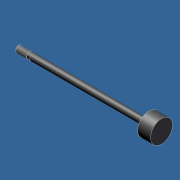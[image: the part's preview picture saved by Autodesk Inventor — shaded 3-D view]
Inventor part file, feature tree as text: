
AUTODESK INVENTOR PART (.ipt)
format: ipt  version: unknown  size: 224,256 bytes
history: native  units: in
note: dims shown in document units (in); Inventor stores cm internally (conversion verified against a paired STEP export)
features: other x98, sketch x3, revolve x2, thread x1, extrude x1
ambient origin geometry x8: Origin, YZ Plane, XZ Plane, XY Plane, X Axis, Y Axis, Z Axis, Center Point
feature tree (105):
  revolve  "Revolution1"  Angle=360.0deg
  revolve  "Revolution2"  [1 undecoded]
  thread  "Thread1"  [1 undecoded]
  extrude  "Extrusion1"  [1 undecoded]
  other  "dia1_XY"
  other  "dia1_YZ"
  other  "dia1_ZX"
  other  "dia1_X"
  other  "dia1_Y"
  other  "dia1_Z"
  other  "dia1_Center"
  other  "dia12_XY"
  other  "dia12_YZ"
  other  "dia12_ZX"
  other  "dia12_X"
  other  "dia12_Y"
  other  "dia12_Z"
  other  "dia12_Center"
  other  "dia2_XY"
  other  "dia2_YZ"
  other  "dia2_ZX"
  other  "dia2_X"
  other  "dia2_Y"
  other  "dia2_Z"
  other  "dia2_Center"
  other  "dia22_XY"
  other  "dia22_YZ"
  other  "dia22_ZX"
  other  "dia22_X"
  other  "dia22_Y"
  other  "dia22_Z"
  other  "dia22_Center"
  other  "rl1_XY"
  other  "rl1_YZ"
  other  "rl1_ZX"
  other  "rl1_X"
  other  "rl1_Y"
  other  "rl1_Z"
  other  "rl1_Center"
  other  "rl2_XY"
  other  "rl2_YZ"
  other  "rl2_ZX"
  other  "rl2_X"
  other  "rl2_Y"
  other  "rl2_Z"
  other  "rl2_Center"
  other  "rod_cp_XY"
  other  "rod_cp_YZ"
  other  "rod_cp_ZX"
  other  "rod_cp_X"
  other  "rod_cp_Y"
  other  "rod_cp_Z"
  other  "rod_cp_Center"
  other  "thd1_XY"
  other  "thd1_YZ"
  other  "thd1_ZX"
  other  "thd1_X"
  other  "thd1_Y"
  other  "thd1_Z"
  other  "thd1_Center"
  other  "thd2_XY"
  other  "thd2_YZ"
  other  "thd2_ZX"
  other  "thd2_X"
  other  "thd2_Y"
  other  "thd2_Z"
  other  "thd2_Center"
  other  "to_rod_clevis_XY"
  other  "to_rod_clevis_YZ"
  other  "to_rod_clevis_ZX"
  other  "to_rod_clevis_X"
  other  "to_rod_clevis_Y"
  other  "to_rod_clevis_Z"
  other  "to_rod_clevis_Center"
  other  "wf1_XY"
  other  "wf1_YZ"
  other  "wf1_ZX"
  other  "wf1_X"
  other  "wf1_Y"
  other  "wf1_Z"
  other  "wf1_Center"
  other  "wf2_XY"
  other  "wf2_YZ"
  other  "wf2_ZX"
  other  "wf2_X"
  other  "wf2_Y"
  other  "wf2_Z"
  other  "wf2_Center"
  other  "wfw1_XY"
  other  "wfw1_YZ"
  other  "wfw1_ZX"
  other  "wfw1_X"
  other  "wfw1_Y"
  other  "wfw1_Z"
  other  "wfw1_Center"
  other  "wfw2_XY"
  other  "wfw2_YZ"
  other  "wfw2_ZX"
  other  "wfw2_X"
  other  "wfw2_Y"
  other  "wfw2_Z"
  other  "wfw2_Center"
  sketch  "Sketch_1"  dims[d0=360.0deg d1=360.0deg]
  sketch  "Sketch_3"  dims[d2=0.75in d3=0.0in d4=0.25in d5=0.0in]
  sketch  "Sketch_10"
note: 3 required parameter values undecoded (feature->parameter linkage not recoverable at this tier; creation-order binding heuristic only, values carry confidence <= 0.55)